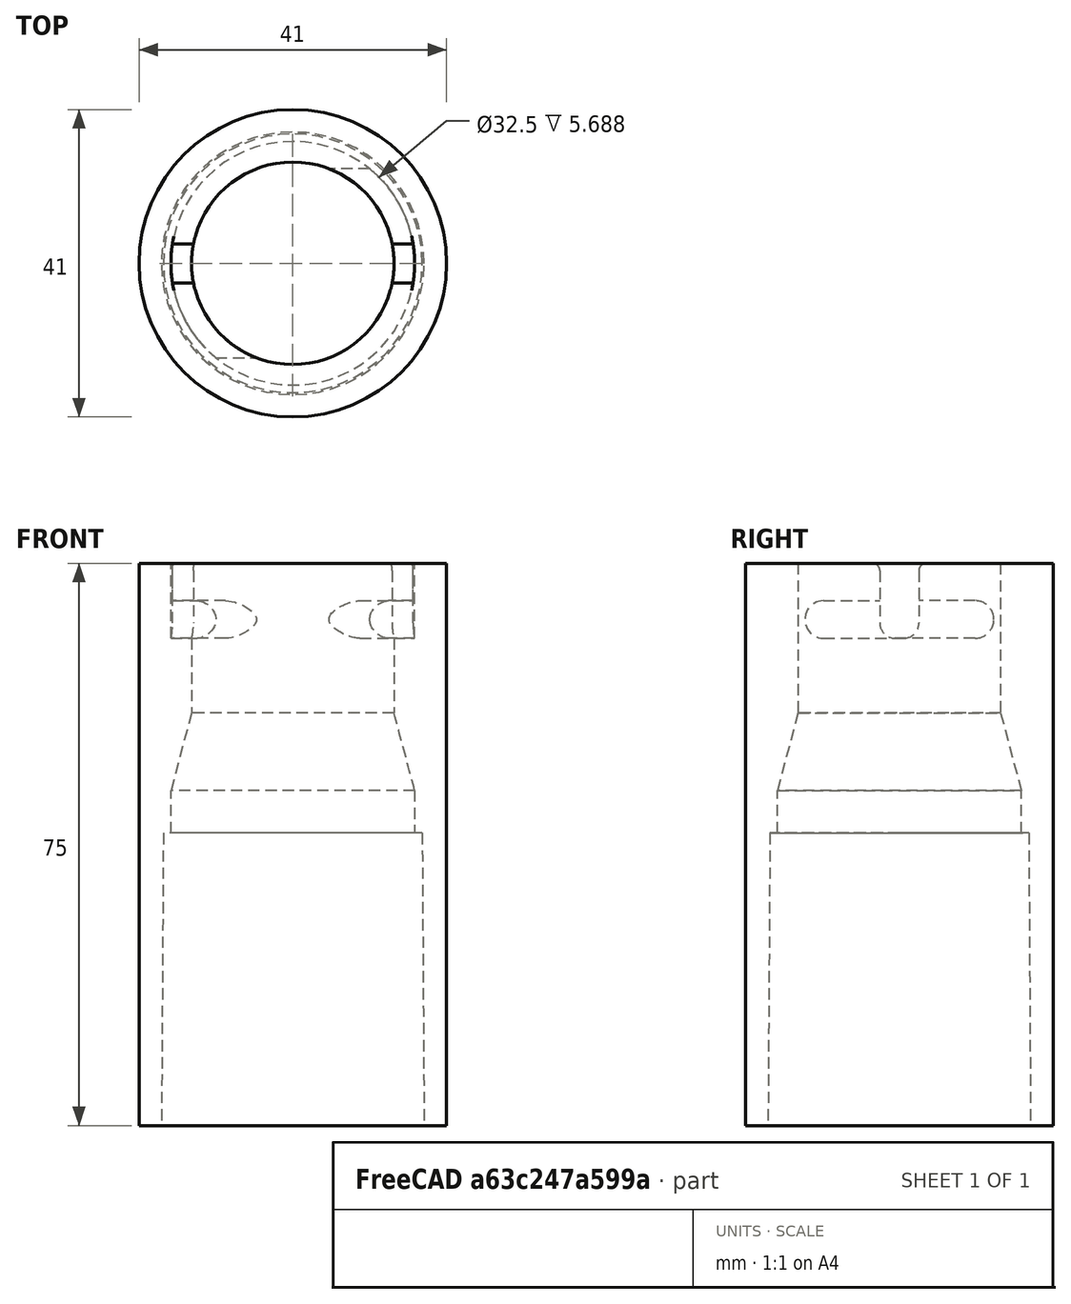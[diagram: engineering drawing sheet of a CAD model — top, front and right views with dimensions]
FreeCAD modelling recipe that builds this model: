
FCSTD DOCUMENT  (FreeCAD 1.1R)
Label: Black_Decker_Vacuum_Adapter
License: All rights reserved
LicenseURL: https://en.wikipedia.org/wiki/All_rights_reserved
objects: Sketcher::SketchObject×9, PartDesign::AdditiveLoft×3, App::Point×2, PartDesign::Pocket×2, Mesh::Feature×1, PartDesign::Pad×1, PartDesign::Body×1
note: 37 computed .brp shape members not serialized (recipe doc carries the construction recipe); baked Part::Feature solids carry a one-line shape summary decoded from their .brp

FEATURE [Mesh::Feature] BLACK_DECKER_and_RIGID_Orbital_Sander_Adapter  label="BLACK+DECKER_and_RIGID_Orbital_Sander_Adapter"
FEATURE [App::Point] Origin001
  Role = Origin
FEATURE [Sketcher::SketchObject] Sketch
  ArcFitTolerance = 1e-06
  AttachmentOffset = pos=(0,0,20) rot=(0,0,1;0rad)
  AttachmentSupport = -> [Origin]
  ExternalTypes = [0]
  FullyConstrained = true
  MakeInternals = false
  MapMode = 5
  Placement = pos=(0,0,20) rot=(0,0,1;0rad)
  sketch-geometry (2):
    g0: Circle CenterX=0 CenterY=0 CenterZ=0 NormalX=0 NormalY=0 NormalZ=1 AngleXU=0 Radius=13.5
    g1: Circle CenterX=0 CenterY=0 CenterZ=0 NormalX=0 NormalY=0 NormalZ=1 AngleXU=0 Radius=16.75
  constraints (4):
    c: Coincident(g0,g-1)
    c: Diameter(g0) = 27
    c: Diameter(g1) = 33.5
    c: Coincident(g1,g0)
FEATURE [Sketcher::SketchObject] Sketch002
  ArcFitTolerance = 1e-06
  AttachmentOffset = pos=(0,0,-35) rot=(0,0,1;0rad)
  AttachmentSupport = -> [Sketch]
  ExternalTypes = [0]
  FullyConstrained = true
  MakeInternals = false
  MapMode = 2
  Placement = pos=(0,0,-15) rot=(0,0,1;0rad)
  sketch-geometry (2):
    g0: Circle CenterX=0 CenterY=0 CenterZ=0 NormalX=0 NormalY=0 NormalZ=1 AngleXU=0 Radius=17.25
    g1: Circle CenterX=0 CenterY=0 CenterZ=0 NormalX=0 NormalY=0 NormalZ=1 AngleXU=0 Radius=20.5
  constraints (4):
    c: Diameter(g0) = 34.5
    c: Coincident(g0,g-1)
    c: Diameter(g1) = 41
    c: Coincident(g1,g0)
FEATURE [App::Point] Origin003
  Role = Origin
FEATURE [Sketcher::SketchObject] Sketch003
  ArcFitTolerance = 1e-06
  AttachmentSupport = -> [Origin002]
  ExternalTypes = [0]
  FullyConstrained = true
  MakeInternals = false
  MapMode = 5
  sketch-geometry (2):
    g0: Circle CenterX=0 CenterY=0 CenterZ=0 NormalX=0 NormalY=0 NormalZ=1 AngleXU=0 Radius=13.5
    g1: Circle CenterX=0 CenterY=0 CenterZ=0 NormalX=0 NormalY=0 NormalZ=1 AngleXU=0 Radius=16.75
  constraints (4):
    c: Coincident(g0,g-1)
    c: Diameter(g0) = 27
    c: Diameter(g1) = 33.5
    c: Coincident(g1,g0)
FEATURE [Sketcher::SketchObject] Sketch005
  ArcFitTolerance = 1e-06
  AttachmentOffset = pos=(0,0,-70) rot=(0,0,1;0rad)
  ExternalTypes = [0]
  FullyConstrained = true
  MakeInternals = false
  MapMode = 2
  Placement = pos=(0,0,-55) rot=(0,0,1;0rad)
  sketch-geometry (2):
    g0: Circle CenterX=0 CenterY=0 CenterZ=0 NormalX=0 NormalY=0 NormalZ=1 AngleXU=0 Radius=17.5
    g1: Circle CenterX=0 CenterY=0 CenterZ=0 NormalX=0 NormalY=0 NormalZ=1 AngleXU=0 Radius=20.5
  constraints (4):
    c: Diameter(g0) = 35
    c: Coincident(g0,g-1)
    c: Diameter(g1) = 41
    c: Coincident(g1,g0)
FEATURE [PartDesign::AdditiveLoft] AdditiveLoft
  Closed = false
  Profile = -> Sketch
  Refine = true
  Ruled = false
  Sections = -> [Sketch003]
  Suppressed = false
FEATURE [Sketcher::SketchObject] Sketch006
  ArcFitTolerance = 1e-06
  AttachmentOffset = pos=(0,0,-35) rot=(0,0,1;0rad)
  AttachmentSupport = -> [Sketch]
  ExternalTypes = [0]
  FullyConstrained = true
  MakeInternals = false
  MapMode = 2
  Placement = pos=(0,0,-15) rot=(0,0,1;0rad)
  sketch-geometry (2):
    g0: Circle CenterX=0 CenterY=0 CenterZ=0 NormalX=0 NormalY=0 NormalZ=1 AngleXU=0 Radius=17.5
    g1: Circle CenterX=0 CenterY=0 CenterZ=0 NormalX=0 NormalY=0 NormalZ=1 AngleXU=0 Radius=20.5
  constraints (4):
    c: Diameter(g0) = 35
    c: Coincident(g0,g-1)
    c: Diameter(g1) = 41
    c: Coincident(g1,g0)
FEATURE [Sketcher::SketchObject] Sketch007
  ArcFitTolerance = 1e-06
  AttachmentSupport = -> [Origin002]
  ExternalTypes = [0]
  FullyConstrained = true
  MakeInternals = false
  MapMode = 5
  sketch-geometry (2):
    g0: Circle CenterX=0 CenterY=0 CenterZ=0 NormalX=0 NormalY=0 NormalZ=1 AngleXU=0 Radius=13.5
    g1: Circle CenterX=0 CenterY=0 CenterZ=0 NormalX=0 NormalY=0 NormalZ=1 AngleXU=0 Radius=16.75
  constraints (4):
    c: Coincident(g0,g-1)
    c: Diameter(g0) = 27
    c: Diameter(g1) = 33.5
    c: Coincident(g1,g0)
FEATURE [PartDesign::AdditiveLoft] AdditiveLoft001
  BaseFeature = -> AdditiveLoft
  Closed = false
  Profile = -> Sketch006
  Refine = true
  Ruled = false
  Sections = -> [Sketch007]
  Suppressed = false
FEATURE [PartDesign::AdditiveLoft] AdditiveLoft002
  BaseFeature = -> AdditiveLoft001
  Closed = false
  Profile = -> Sketch002
  Refine = true
  Ruled = false
  Sections = -> [Sketch005]
  Suppressed = false
FEATURE [Sketcher::SketchObject] Sketch008
  ArcFitTolerance = 1e-06
  AttachmentSupport = -> [Origin]
  ExternalTypes = [0]
  FullyConstrained = false
  MakeInternals = false
  MapMode = 5
  Placement = pos=(0,0,0) rot=(0.57735,0.57735,0.57735;2.0944rad)
  sketch-geometry (12):
    g0: ArcOfCircle CenterX=3.6 CenterY=19 CenterZ=0 NormalX=0 NormalY=0 NormalZ=1 AngleXU=0 Radius=1 StartAngle=1.5708 EndAngle=3.14159
    g1: ArcOfCircle CenterX=-3.6 CenterY=19 CenterZ=0 NormalX=0 NormalY=0 NormalZ=1 AngleXU=0 Radius=1 StartAngle=9e-16 EndAngle=1.5708
    g2: LineSegment StartX=0.6 StartY=10 StartZ=0 EndX=-10.1 EndY=10 EndZ=0
    g3: LineSegment StartX=-2.6 StartY=19 StartZ=0 EndX=-2.6 EndY=15 EndZ=0
    g4: LineSegment StartX=-2.6 StartY=15 StartZ=0 EndX=-10.1 EndY=15 EndZ=0
    g5: LineSegment StartX=-3.6 StartY=20 StartZ=0 EndX=-7.02897 EndY=22.3136 EndZ=0
    g6: LineSegment StartX=-7.02897 StartY=22.3136 StartZ=0 EndX=8.77367 EndY=22.3136 EndZ=0
    g7: LineSegment StartX=8.77367 StartY=22.3136 StartZ=0 EndX=3.6 EndY=20 EndZ=0
    g8: ArcOfCircle CenterX=-10.1 CenterY=12.5 CenterZ=0 NormalX=0 NormalY=0 NormalZ=1 AngleXU=0 Radius=2.5 StartAngle=1.5708 EndAngle=4.71239
    g9: LineSegment StartX=2.6 StartY=19 StartZ=0 EndX=2.6 EndY=12 EndZ=0
    g10: ArcOfCircle CenterX=0.6 CenterY=12 CenterZ=0 NormalX=0 NormalY=0 NormalZ=1 AngleXU=0 Radius=2 StartAngle=4.71239 EndAngle=6.28319
    g11: GeomPoint [constr] X=2.6 Y=10 Z=0
  constraints (32):
    c: Radius(g0) = 1
    c: Angle(g0) = 1.5708
    c: Angle(g1) = 1.5708
    c: Symmetric(g0,g1,g-2)
    c: Symmetric(g0,g1,g-2)
    c: Horizontal(g0,g0)
    c: Distance(g0,g-2) = 2.6
    c: Horizontal(g2)
    c: Coincident(g3,g1)
    c: Vertical(g3)
    c: Coincident(g3,g4)
    c: Horizontal(g4)
    c: Coincident(g5,g1)
    c: Coincident(g5,g6)
    c: Horizontal(g6)
    c: Coincident(g6,g7)
    c: Coincident(g7,g0)
    c: Coincident(g8,g4)
    c: Coincident(g8,g2)
    c: Vertical(g2,g8)
    c: Vertical(g4,g8)
    c: Distance(g0,g-1) = 20
    c: DistanceY(g3,g3) = 4
    c: DistanceX(g4,g4) = 7.5
    c: Distance(g2,g4) = 5
    c: Coincident(g9,g0)
    c: Perpendicular(g9,g2)
    c: PointOnObject(g11,g2)
    c: PointOnObject(g11,g9)
    c: Tangent(g2,g10) = 1.5708
    c: Tangent(g9,g10) = 1.5708
    c: Distance(g2,g11) = 2
FEATURE [PartDesign::Pocket] Pocket
  BaseFeature = -> AdditiveLoft002
  Direction = (-1,0,0)
  Length = 200
  Length2 = 5
  Profile = -> Sketch008
  ReferenceAxis = -> Sketch008 [N_Axis]
  Refine = true
  SideType = 0
  Suppressed = false
  Type = 0
  Type2 = 0
FEATURE [Sketcher::SketchObject] Sketch009
  ArcFitTolerance = 1e-06
  AttachmentSupport = -> [Origin]
  ExternalTypes = [0]
  FullyConstrained = false
  MakeInternals = false
  MapMode = 5
  Placement = pos=(0,0,0) rot=(0.57735,0.57735,0.57735;2.0944rad)
  sketch-geometry (13):
    g0: GeomPoint [constr] X=2.6 Y=6.24789 Z=0
    g1: ArcOfCircle CenterX=-3.6 CenterY=19 CenterZ=0 NormalX=0 NormalY=0 NormalZ=1 AngleXU=0 Radius=1 StartAngle=0 EndAngle=1.5708
    g2: ArcOfCircle CenterX=3.6 CenterY=19 CenterZ=0 NormalX=0 NormalY=0 NormalZ=1 AngleXU=0 Radius=1 StartAngle=1.5708 EndAngle=3.14159
    g3: LineSegment StartX=-0.6 StartY=10 StartZ=0 EndX=10.1 EndY=10 EndZ=0
    g4: LineSegment StartX=2.6 StartY=19 StartZ=0 EndX=2.6 EndY=15 EndZ=0
    g5: LineSegment StartX=2.6 StartY=15 StartZ=0 EndX=10.1 EndY=15 EndZ=0
    g6: LineSegment StartX=3.6 StartY=20 StartZ=0 EndX=7.02897 EndY=22.3136 EndZ=0
    g7: LineSegment StartX=7.02897 StartY=22.3136 StartZ=0 EndX=-8.77367 EndY=22.3136 EndZ=0
    g8: LineSegment StartX=-8.77367 StartY=22.3136 StartZ=0 EndX=-3.6 EndY=20 EndZ=0
    g9: ArcOfCircle CenterX=10.1 CenterY=12.5 CenterZ=0 NormalX=0 NormalY=0 NormalZ=1 AngleXU=0 Radius=2.5 StartAngle=4.71239 EndAngle=7.85398
    g10: LineSegment StartX=-2.6 StartY=19 StartZ=0 EndX=-2.6 EndY=12 EndZ=0
    g11: ArcOfCircle CenterX=-0.6 CenterY=12 CenterZ=0 NormalX=0 NormalY=0 NormalZ=1 AngleXU=0 Radius=2 StartAngle=3.14159 EndAngle=4.71239
    g12: GeomPoint [constr] X=-2.6 Y=10 Z=0
  constraints (23):
    c: Radius(g1) = 1
    c: Angle(g1) = 1.5708
    c: Angle(g2) = 1.5708
    c: Horizontal(g3)
    c: Coincident(g4,g2)
    c: Vertical(g4)
    c: Coincident(g4,g5)
    c: Horizontal(g5)
    c: Coincident(g6,g2)
    c: Coincident(g6,g7)
    c: Horizontal(g7)
    c: Coincident(g7,g8)
    c: Coincident(g8,g1)
    c: Coincident(g9,g5)
    c: Coincident(g9,g3)
    c: Distance(g3,g5) = 5
    c: Coincident(g10,g1)
    c: Perpendicular(g10,g3)
    c: PointOnObject(g12,g3)
    c: PointOnObject(g12,g10)
    c: Tangent(g3,g11) = -1.5708
    c: Tangent(g10,g11) = -1.5708
    c: Distance(g3,g12) = 2
FEATURE [PartDesign::Pocket] Pocket001
  BaseFeature = -> Pocket
  Direction = (-1,0,0)
  Length = 20
  Length2 = 5
  Profile = -> Sketch009
  ReferenceAxis = -> Sketch009 [N_Axis]
  Refine = true
  Reversed = true
  SideType = 0
  Suppressed = false
  Type = 0
  Type2 = 0
FEATURE [Sketcher::SketchObject] Sketch010
  ArcFitTolerance = 1e-06
  AttachmentSupport = -> [Origin]
  ExternalTypes = [0]
  FullyConstrained = true
  MakeInternals = false
  MapMode = 5
  sketch-geometry (2):
    g0: Circle CenterX=0 CenterY=0 CenterZ=0 NormalX=0 NormalY=0 NormalZ=1 AngleXU=0 Radius=16.25
    g1: Circle CenterX=0 CenterY=0 CenterZ=0 NormalX=0 NormalY=0 NormalZ=1 AngleXU=0 Radius=20.5
  constraints (4):
    c: Coincident(g0,g-1)
    c: Coincident(g1,g0)
    c: Diameter(g0) = 32.5
    c: Diameter(g1) = 41
FEATURE [PartDesign::Pad] Pad
  BaseFeature = -> Pocket001
  Direction = (0,0,1)
  Length = 20
  Length2 = 16
  Profile = -> Sketch010
  ReferenceAxis = -> Sketch010 [N_Axis]
  Refine = true
  SideType = 1
  Suppressed = false
  Type = 0
  Type2 = 0
FEATURE [PartDesign::Body] Body
  AllowCompound = false
  Group = -> [Sketch,Sketch003,Sketch002,Sketch005,AdditiveLoft,Sketch006,Sketch007,AdditiveLoft001,AdditiveLoft002,Sketch008,Pocket,Sketch009,Pocket001,Sketch010,Pad]
  Origin = -> Origin
  Tip = -> Pad
